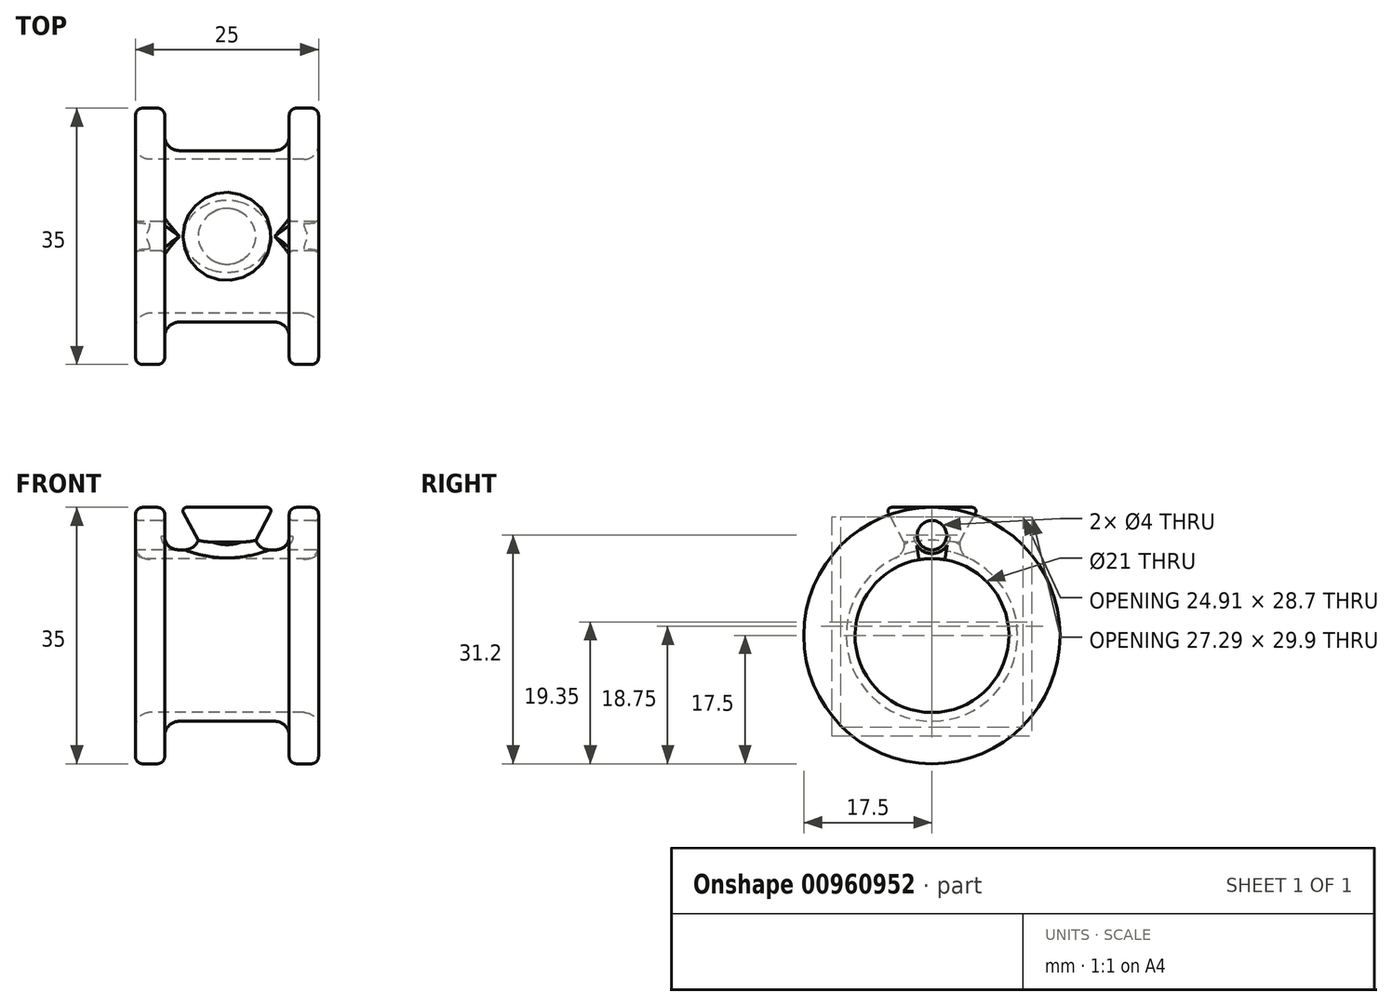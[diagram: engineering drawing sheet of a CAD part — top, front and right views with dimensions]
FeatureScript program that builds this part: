
annotation { "Feature Type Name" : "Feature", "Feature Type Description" : "" }
export const myFeature = defineFeature(function(context is Context, id is Id, definition is map)
    precondition{}
    {
        {
            var Q0;
            Q0=qCreatedBy(makeId("Right.planeOp"),FACE);
            var sketch = newSketch(context, id + "F0", { "sketchPlane" : qUnion([Q0])});
            skCircle(sketch, "E0", {"center": v(0, 0) * mm, "radius": 10.5 * mm});
            skCircle(sketch, "E1.0", {"center": v(0, 0) * mm, "radius": 11.7 * mm});
            skCircle(sketch, "E2.0", {"center": v(0, 0) * mm, "radius": 17.5 * mm});
            skLineSegment(sketch, "E3", {"start": v(0, 17.5) * mm, "end": v(0, 11.7) * mm, "construction": true});
            skCircle(sketch, "E4", {"center": v(0, 13.7) * mm, "radius": 2 * mm});
            skLineSegment(sketch, "E5", {"start": v(4.15, 11.49) * mm, "end": v(-6.29, 11.49) * mm, "construction": true});
            skPoint(sketch, "E6", {"position": v(0, 11.49) * mm});
            skSolve(sketch);
        }
        {
            var Q0;
            Q0=makeQuery(id+"F0.imprint","IMPRINT",FACE,{"disambiguationData":[TD([[makeQuery(id+"F0.imprint","IMPRINT",EDGE,{"derivedFrom":sQuery(id+"F0.wireOp",EDGE,"E1.0")}),-1.0]])]});
            var Q1;
            Q1=makeQuery(id+"F0.imprint","IMPRINT",FACE,{"disambiguationData":[TD([[makeQuery(id+"F0.imprint","IMPRINT",EDGE,{"derivedFrom":sQuery(id+"F0.wireOp",EDGE,"E0")}),-1.0]])]});
            extrude(context, id + "F1", {"entities" : qUnion([Q0, Q1]), "endBound" : BoundingType.SYMMETRIC, "depth" : 25 * mm, "offsetDistance" : 25 * mm});
        }
        {
            var Q0;
            Q0=makeQuery(id+"F0.imprint","IMPRINT",FACE,{"disambiguationData":[TD([[makeQuery(id+"F0.imprint","IMPRINT",EDGE,{"derivedFrom":sQuery(id+"F0.wireOp",EDGE,"E1.0")}),-1.0]])]});
            var Q1;
            Q1=makeQuery(id+"F0.imprint","IMPRINT",FACE,{"disambiguationData":[TD([[makeQuery(id+"F0.imprint","IMPRINT",EDGE,{"derivedFrom":sQuery(id+"F0.wireOp",EDGE,"E4")}),1.0]])]});
            var Q2;
            Q2=makeQuery(id+"F1.opExtrude","CAP_FACE",FACE,{"disambiguationData":[OSD([sQuery(id+"F0.wireOp",EDGE,"E0"),sQuery(id+"F0.wireOp",EDGE,"E2.0"),sQuery(id+"F0.wireOp",EDGE,"E4")])],"isStart":true});
            var Q3;
            Q3=makeQuery(id+"F1.opExtrude","CAP_FACE",FACE,{"disambiguationData":[OSD([sQuery(id+"F0.wireOp",EDGE,"E0"),sQuery(id+"F0.wireOp",EDGE,"E2.0"),sQuery(id+"F0.wireOp",EDGE,"E4")])],"isStart":false});
            extrude(context, id + "F2", {"entities" : qUnion([Q0, Q1]), "operationType" : NewBodyOperationType.REMOVE, "endBound" : BoundingType.UP_TO_SURFACE, "oppositeDirection" : true, "depth" : 25 * mm, "endBoundEntityFace" : qUnion([Q2]), "hasOffset" : true, "offsetDistance" : 4 * mm, "hasSecondDirection" : true, "secondDirectionBound" : SecondDirectionBoundingType.UP_TO_SURFACE, "secondDirectionOppositeDirection" : false, "secondDirectionDepth" : 25 * mm, "secondDirectionBoundEntityFace" : qUnion([Q3]), "hasSecondDirectionOffset" : true, "secondDirectionOffsetDistance" : 4 * mm});
        }
        {
            var Q0;
            Q0=qCreatedBy(makeId("Front.planeOp"),FACE);
            var sketch = newSketch(context, id + "F3", { "sketchPlane" : qUnion([Q0])});
            skLineSegment(sketch, "E7", {"start": v(-6.35, 17.5) * mm, "end": v(-3.8, 12.78) * mm});
            skLineSegment(sketch, "E8", {"start": v(-3.8, 12.78) * mm, "end": v(-3.8, 11.14) * mm});
            skLineSegment(sketch, "E9", {"start": v(0, 17.5) * mm, "end": v(-6.35, 17.5) * mm});
            skLineSegment(sketch, "E10", {"start": v(-3.8, 11.14) * mm, "end": v(0, 11.14) * mm});
            skLineSegment(sketch, "E11", {"start": v(0, 11.14) * mm, "end": v(0, 17.5) * mm});
            skSolve(sketch);
        }
        {
            var Q0;
            Q0=makeQuery(id+"F3.imprint","IMPRINT",FACE,{"disambiguationData":[TD([[makeQuery(id+"F3.imprint","IMPRINT",EDGE,{"derivedFrom":sQuery(id+"F3.wireOp",EDGE,"E7")}),1.0]])]});
            var Q1;
            Q1 = qConstructionFilter(qBodyType(qCreatedBy(id + "F3" ,EDGE), BodyType.WIRE), ConstructionObject.NO);
            var Q2;
            Q2=sQuery(id+"F0.wireOp",EDGE,"E3");
            revolve(context, id + "F4", {"operationType" : NewBodyOperationType.ADD, "surfaceOperationType" : NewSurfaceOperationType.NEW, "entities" : qUnion([Q0]), "surfaceEntities" : qUnion([Q1]), "axis" : qUnion([Q2]), "revolveType" : RevolveType.FULL, "oppositeDirection" : true});
        }
        {
            var Q0;
            Q0=makeQuery(id+"F2.boolean.opBoolean","COPY",FACE,{"derivedFrom":makeQuery(id+"F2.opExtrude","SWEPT_FACE",FACE,{"disambiguationData":[OSD([sQuery(id+"F0.wireOp",EDGE,"E1.0")])]})});
            fillet(context, id + "F5", {"entities" : qUnion([Q0]), "radius" : 2 * mm, "allowEdgeOverflow" : false});
        }
        {
            var Q0;
            {var subQ0=sQuery(id+"F0.wireOp",EDGE,"E2.0");Q0=makeQuery(id+"F2.boolean.opBoolean","SPLIT",FACE,{"disambiguationData":[TD([makeQuery(id+"F2.opExtrude","CAP_FACE",FACE,{"disambiguationData":[OSD([sQuery(id+"F0.wireOp",EDGE,"E1.0"),subQ0])],"isStart":true})])],"derivedFrom":makeQuery(id+"F1.opExtrude","SWEPT_FACE",FACE,{"disambiguationData":[OSD([subQ0])]})});}
            var Q1;
            {var subQ0=sQuery(id+"F0.wireOp",EDGE,"E2.0");Q1=makeQuery(id+"F2.boolean.opBoolean","SPLIT",FACE,{"disambiguationData":[TD([makeQuery(id+"F2.opExtrude","CAP_FACE",FACE,{"disambiguationData":[OSD([sQuery(id+"F0.wireOp",EDGE,"E1.0"),subQ0])],"isStart":false})])],"derivedFrom":makeQuery(id+"F1.opExtrude","SWEPT_FACE",FACE,{"disambiguationData":[OSD([subQ0])]})});}
            fillet(context, id + "F6", {"entities" : qUnion([Q0, Q1]), "radius" : 1 * mm, "tangentPropagation" : true, "allowEdgeOverflow" : false});
        }
        {
            var Q0;
            Q0=makeQuery(id+"F4.opRevolve","SWEPT_FACE",FACE,{"disambiguationData":[OSD([sQuery(id+"F3.wireOp",EDGE,"E9")])]});
            var Q1;
            {var subQ0=sQuery(id+"F0.wireOp",EDGE,"E4");var subQ1=sQuery(id+"F0.wireOp",EDGE,"E2.0");var subQ2=sQuery(id+"F0.wireOp",EDGE,"E1.0");Q1=makeQuery(id+"F2.boolean.opBoolean","SPLIT",FACE,{"disambiguationData":[TD([makeQuery(id+"F2.opExtrude","CAP_FACE",FACE,{"disambiguationData":[OSD([subQ2,subQ1])],"isStart":true})])],"derivedFrom":makeQuery(id+"F1.opExtrude","SWEPT_FACE",FACE,{"disambiguationData":[OSD([subQ0])]})});}
            var Q2;
            {var subQ0=sQuery(id+"F0.wireOp",EDGE,"E4");var subQ1=sQuery(id+"F0.wireOp",EDGE,"E2.0");var subQ2=sQuery(id+"F0.wireOp",EDGE,"E1.0");Q2=makeQuery(id+"F2.boolean.opBoolean","SPLIT",FACE,{"disambiguationData":[TD([makeQuery(id+"F2.opExtrude","CAP_FACE",FACE,{"disambiguationData":[OSD([subQ2,subQ1])],"isStart":false})])],"derivedFrom":makeQuery(id+"F1.opExtrude","SWEPT_FACE",FACE,{"disambiguationData":[OSD([subQ0])]})});}
            fillet(context, id + "F7", {"entities" : qUnion([Q0, Q1, Q2]), "radius" : 0.5 * mm, "tangentPropagation" : true, "allowEdgeOverflow" : false});
        }
        {
            var Q0;
            Q0=makeQuery(id+"F1.opExtrude","SWEPT_FACE",FACE,{"disambiguationData":[OSD([sQuery(id+"F0.wireOp",EDGE,"E0")])]});
            fillet(context, id + "F8", {"entities" : qUnion([Q0]), "radius" : 2 * mm, "tangentPropagation" : true, "allowEdgeOverflow" : false});
        }
    });
